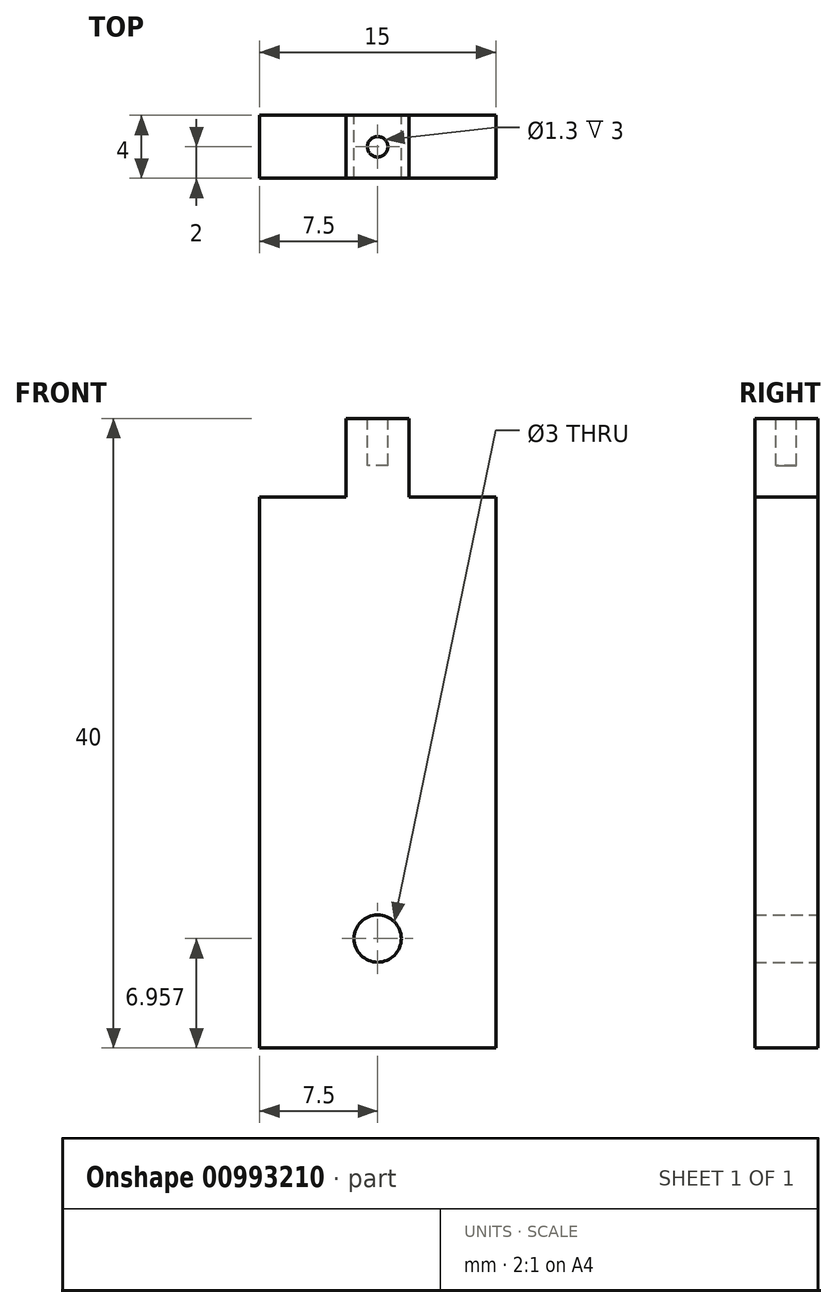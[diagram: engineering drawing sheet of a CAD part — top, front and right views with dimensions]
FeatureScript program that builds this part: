
annotation { "Feature Type Name" : "Feature", "Feature Type Description" : "" }
export const myFeature = defineFeature(function(context is Context, id is Id, definition is map)
    precondition{}
    {
        {
            var Q0;
            Q0=qCreatedBy(makeId("Front.planeOp"),FACE);
            var sketch = newSketch(context, id + "F0", { "sketchPlane" : qUnion([Q0])});
            skLineSegment(sketch, "E0.top", {"start": v(7.5, -12.5) * mm, "end": v(-7.5, -12.5) * mm});
            skLineSegment(sketch, "E0.left", {"start": v(7.5, 22.5) * mm, "end": v(7.5, -12.5) * mm});
            skLineSegment(sketch, "E0.right", {"start": v(-7.5, 22.5) * mm, "end": v(-7.5, -12.5) * mm});
            skLineSegment(sketch, "E1.top", {"start": v(2, 27.5) * mm, "end": v(-2, 27.5) * mm});
            skCircle(sketch, "E2", {"center": v(0, -5.54) * mm, "radius": 1.5 * mm});
            skLineSegment(sketch, "E3.left", {"start": v(2, 27.5) * mm, "end": v(2, 22.5) * mm});
            skLineSegment(sketch, "E3.right", {"start": v(-2, 27.5) * mm, "end": v(-2, 22.5) * mm});
            skPoint(sketch, "E3.middle", {"position": v(0, 14.96) * mm});
            skLineSegment(sketch, "E4", {"start": v(-7.5, 22.5) * mm, "end": v(-2, 22.5) * mm});
            skPoint(sketch, "E3.top.end.orphan", {"position": v(-2, 2.43) * mm});
            skPoint(sketch, "E3.top.start.orphan", {"position": v(2, 2.43) * mm});
            skLineSegment(sketch, "E5.trimOffspring", {"start": v(2, 22.5) * mm, "end": v(7.5, 22.5) * mm});
            skSolve(sketch);
        }
        {
            var Q0;
            Q0 = qSketchRegion(id + "F0", true);
            extrude(context, id + "F1", {"entities" : qUnion([Q0]), "depth" : 4 * mm, "offsetDistance" : 25 * mm});
        }
        {
            var Q0;
            Q0 = qSketchRegion(id + "F0", true);
            extrude(context, id + "F2", {"entities" : qUnion([Q0]), "operationType" : NewBodyOperationType.ADD, "depth" : 4 * mm, "offsetDistance" : 25 * mm});
        }
        {
            var Q0;
            Q0=makeQuery(id+"F1.opExtrude","SWEPT_FACE",FACE,{"disambiguationData":[OSD([sQuery(id+"F0.wireOp",EDGE,"E1.top")])]});
            var sketch = newSketch(context, id + "F3", { "sketchPlane" : qUnion([Q0])});
            skCircle(sketch, "E6", {"center": v(0, -2) * mm, "radius": 0.65 * mm});
            skPoint(sketch, "E6.centerSnap0", {"position": v(2, -2) * mm});
            skSolve(sketch);
        }
        {
            var Q0;
            Q0 = qSketchRegion(id + "F3", true);
            extrude(context, id + "F4", {"entities" : qUnion([Q0]), "operationType" : NewBodyOperationType.REMOVE, "oppositeDirection" : true, "depth" : 3 * mm, "offsetDistance" : 25 * mm});
        }
    });
